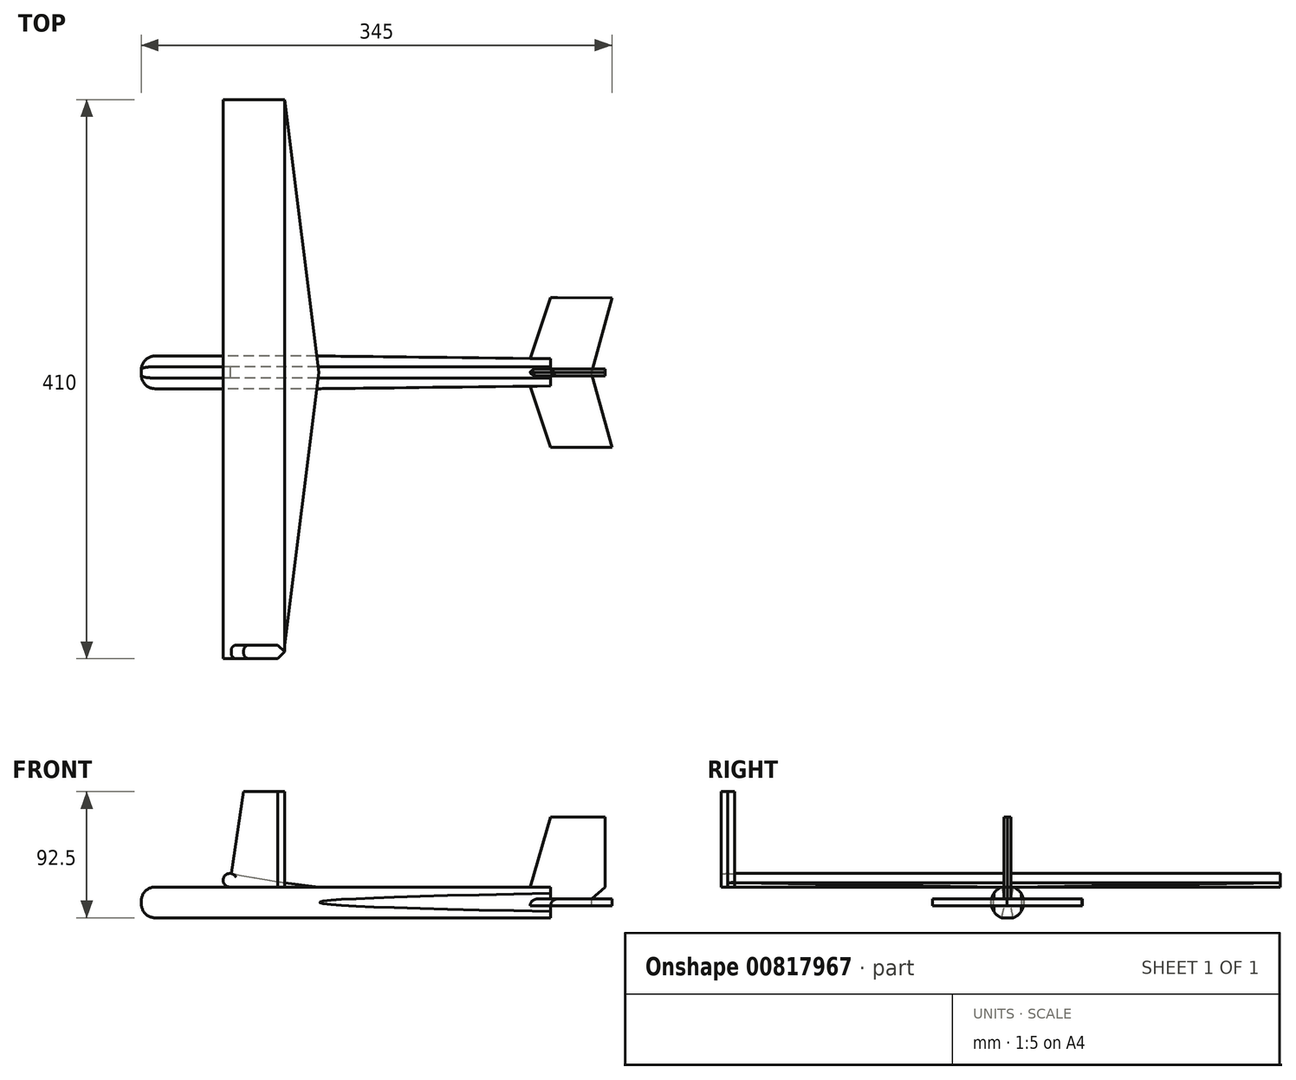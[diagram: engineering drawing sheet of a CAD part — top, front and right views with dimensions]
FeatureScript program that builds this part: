
annotation { "Feature Type Name" : "Feature", "Feature Type Description" : "" }
export const myFeature = defineFeature(function(context is Context, id is Id, definition is map)
    precondition{}
    {
        {
            var Q0;
            Q0=qCreatedBy(makeId("Top.planeOp"),FACE);
            var sketch = newSketch(context, id + "F0", { "sketchPlane" : qUnion([Q0])});
            skLineSegment(sketch, "E0", {"start": v(0, 0) * mm, "end": v(0, 200) * mm});
            skLineSegment(sketch, "E1", {"start": v(0, 0) * mm, "end": v(0, -200) * mm});
            skLineSegment(sketch, "E2", {"start": v(0, -200) * mm, "end": v(45, -200) * mm});
            skLineSegment(sketch, "E3", {"start": v(0, 200) * mm, "end": v(45, 200) * mm});
            skLineSegment(sketch, "E4", {"start": v(0, 0) * mm, "end": v(70, 0) * mm, "construction": true});
            skLineSegment(sketch, "E5", {"start": v(45, 200) * mm, "end": v(70, 0) * mm});
            skLineSegment(sketch, "E6", {"start": v(45, -200) * mm, "end": v(70, 0) * mm});
            skSolve(sketch);
        }
        {
            var Q0;
            Q0=makeQuery(id+"F0.imprint","IMPRINT",FACE,{"disambiguationData":[TD([[makeQuery(id+"F0.imprint","IMPRINT",EDGE,{"derivedFrom":sQuery(id+"F0.wireOp",EDGE,"E0")}),-1.0]])]});
            extrude(context, id + "F1", {"entities" : qUnion([Q0]), "depth" : 10 * mm, "offsetDistance" : 25 * mm});
        }
        {
            var Q0;
            Q0=makeQuery(id+"F1.opExtrude","SWEPT_FACE",FACE,{"disambiguationData":[OSD([sQuery(id+"F0.wireOp",EDGE,"E2")])]});
            var sketch = newSketch(context, id + "F2", { "sketchPlane" : qUnion([Q0])});
            skLineSegment(sketch, "E7.0.0", {"start": v(0, 0) * mm, "end": v(45, 0) * mm});
            skLineSegment(sketch, "E7.0.1", {"start": v(45, 0) * mm, "end": v(45, 10) * mm});
            skLineSegment(sketch, "E7.0.2", {"start": v(45, 10) * mm, "end": v(0, 10) * mm});
            skLineSegment(sketch, "E7.0.3", {"start": v(0, 10) * mm, "end": v(0, 5) * mm});
            skLineSegment(sketch, "E8.0.0", {"start": v(45, 0) * mm, "end": v(70, 0) * mm});
            skLineSegment(sketch, "E8.0.1", {"start": v(70, 0) * mm, "end": v(70, 10) * mm});
            skLineSegment(sketch, "E8.0.2", {"start": v(70, 10) * mm, "end": v(45, 10) * mm});
            skLineSegment(sketch, "E8.0.3", {"start": v(45, 10) * mm, "end": v(45, 0) * mm});
            skArc(sketch, "E9", {"start": v(5.87, 9.92) * mm, "mid": v(0.02, 5.44) * mm, "end": v(5, 0) * mm});
            skPoint(sketch, "E9.centerSnap0", {"position": v(0, 5) * mm});
            skLineSegment(sketch, "E10", {"start": v(5.87, 9.92) * mm, "end": v(45, 3) * mm});
            skLineSegment(sketch, "E11", {"start": v(45, 3) * mm, "end": v(70, 0) * mm});
            skSolve(sketch);
        }
        {
            var Q0;
            {var subQ5=sQuery(id+"F2.wireOp",EDGE,"E10");Q0=makeQuery(id+"F2.imprint","IMPRINT",FACE,{"disambiguationData":[TD([[makeQuery(id+"F2.imprint","IMPRINT",EDGE,{"derivedFrom":subQ5}),1.0]])]});}
            var Q1;
            Q1=makeQuery(id+"F2.imprint","IMPRINT",FACE,{"disambiguationData":[TD([[makeQuery(id+"F2.imprint","IMPRINT",EDGE,{"derivedFrom":sQuery(id+"F2.wireOp",EDGE,"E8.0.1")}),1.0]])]});
            var Q2;
            {var subQ0=sQuery(id+"F2.wireOp",EDGE,"E7.0.3");Q2=makeQuery(id+"F2.imprint","IMPRINT",FACE,{"disambiguationData":[TD([[makeQuery(id+"F2.imprint","IMPRINT",EDGE,{"derivedFrom":subQ0}),1.0]])]});}
            var Q3;
            {var subQ0=sQuery(id+"F2.wireOp",EDGE,"E7.0.0");var subQ3=sQuery(id+"F2.wireOp",EDGE,"E9");var subQ4=makeQuery(id+"F2.imprint","INTERSECT",VERTEX,{"derivedFrom":[subQ0,subQ3]});Q3=makeQuery(id+"F2.imprint","IMPRINT",FACE,{"disambiguationData":[TD([[makeQuery(id+"F2.imprint","IMPRINT",EDGE,{"disambiguationData":[TD([[subQ4,1.0]])],"derivedFrom":subQ0}),1.0]])]});}
            extrude(context, id + "F3", {"entities" : qUnion([Q0, Q1, Q2, Q3]), "operationType" : NewBodyOperationType.REMOVE, "oppositeDirection" : true, "depth" : 400 * mm, "offsetDistance" : 25 * mm});
        }
        {
            var Q0;
            Q0=qCreatedBy(makeId("Top.planeOp"),FACE);
            var sketch = newSketch(context, id + "F4", { "sketchPlane" : qUnion([Q0])});
            skLineSegment(sketch, "E12", {"start": v(0, 12) * mm, "end": v(0, -12) * mm});
            skLineSegment(sketch, "E13", {"start": v(0, -12) * mm, "end": v(-60, -12) * mm});
            skLineSegment(sketch, "E14", {"start": v(-60, -12) * mm, "end": v(-60, 12) * mm});
            skLineSegment(sketch, "E15", {"start": v(-60, 12) * mm, "end": v(0, 12) * mm});
            skLineSegment(sketch, "E16", {"start": v(0, -12) * mm, "end": v(70, -12) * mm});
            skLineSegment(sketch, "E17", {"start": v(70, -12) * mm, "end": v(70, 12) * mm});
            skLineSegment(sketch, "E18", {"start": v(70, 12) * mm, "end": v(0, 12) * mm});
            skLineSegment(sketch, "E19", {"start": v(0, 0) * mm, "end": v(240, 0) * mm, "construction": true});
            skPoint(sketch, "E19.endSnap0", {"position": v(70, 0) * mm});
            skLineSegment(sketch, "E20", {"start": v(240, -10) * mm, "end": v(240, 10) * mm});
            skLineSegment(sketch, "E21", {"start": v(240, -10) * mm, "end": v(70, -12) * mm});
            skLineSegment(sketch, "E22", {"start": v(70, 12) * mm, "end": v(240, 10) * mm});
            skSolve(sketch);
        }
        {
            var Q0;
            Q0=makeQuery(id+"F4.imprint","IMPRINT",FACE,{"disambiguationData":[TD([[makeQuery(id+"F4.imprint","IMPRINT",EDGE,{"derivedFrom":sQuery(id+"F4.wireOp",EDGE,"E12")}),1.0]])]});
            var Q1;
            Q1=makeQuery(id+"F4.imprint","IMPRINT",FACE,{"disambiguationData":[TD([[makeQuery(id+"F4.imprint","IMPRINT",EDGE,{"derivedFrom":sQuery(id+"F4.wireOp",EDGE,"E12")}),-1.0]])]});
            var Q2;
            Q2=makeQuery(id+"F4.imprint","IMPRINT",FACE,{"disambiguationData":[TD([[makeQuery(id+"F4.imprint","IMPRINT",EDGE,{"derivedFrom":sQuery(id+"F4.wireOp",EDGE,"E17")}),-1.0]])]});
            extrude(context, id + "F5", {"entities" : qUnion([Q0, Q1, Q2]), "operationType" : NewBodyOperationType.ADD, "oppositeDirection" : true, "depth" : 22.5 * mm, "offsetDistance" : 25 * mm});
        }
        {
            var Q0;
            Q0=makeQuery(id+"F5.opExtrude","SWEPT_FACE",FACE,{"disambiguationData":[OSD([sQuery(id+"F4.wireOp",EDGE,"E14")])]});
            var sketch = newSketch(context, id + "F6", { "sketchPlane" : qUnion([Q0])});
            skLineSegment(sketch, "E23.0.0", {"start": v(12, 0) * mm, "end": v(-12, 0) * mm});
            skLineSegment(sketch, "E23.0.1", {"start": v(-12, 0) * mm, "end": v(-12, -22.5) * mm});
            skLineSegment(sketch, "E23.0.2", {"start": v(-12, -22.5) * mm, "end": v(12, -22.5) * mm});
            skLineSegment(sketch, "E23.0.3", {"start": v(12, -22.5) * mm, "end": v(12, 0) * mm});
            skCircle(sketch, "E24", {"center": v(0, -11.25) * mm, "radius": 12 * mm});
            skPoint(sketch, "E24.centerSnap0", {"position": v(-12, -11.25) * mm});
            skSolve(sketch);
        }
        {
            var Q0;
            {var subQ0=sQuery(id+"F6.wireOp",EDGE,"E23.0.1");var subQ1=sQuery(id+"F6.wireOp",EDGE,"E23.0.0");var subQ2=makeQuery(id+"F6.imprint","INTERSECT",VERTEX,{"derivedFrom":[subQ1,subQ0]});Q0=makeQuery(id+"F6.imprint","IMPRINT",FACE,{"disambiguationData":[TD([[makeQuery(id+"F6.imprint","IMPRINT",EDGE,{"disambiguationData":[TD([[subQ2,1.0]])],"derivedFrom":subQ1}),1.0]])]});}
            var Q1;
            {var subQ0=sQuery(id+"F6.wireOp",EDGE,"E23.0.3");var subQ1=sQuery(id+"F6.wireOp",EDGE,"E23.0.0");var subQ2=makeQuery(id+"F6.imprint","INTERSECT",VERTEX,{"derivedFrom":[subQ1,subQ0]});Q1=makeQuery(id+"F6.imprint","IMPRINT",FACE,{"disambiguationData":[TD([[makeQuery(id+"F6.imprint","IMPRINT",EDGE,{"disambiguationData":[TD([[subQ2,-1.0]])],"derivedFrom":subQ1}),1.0]])]});}
            var Q2;
            {var subQ0=sQuery(id+"F6.wireOp",EDGE,"E23.0.3");var subQ1=sQuery(id+"F6.wireOp",EDGE,"E23.0.2");var subQ2=makeQuery(id+"F6.imprint","INTERSECT",VERTEX,{"derivedFrom":[subQ1,subQ0]});Q2=makeQuery(id+"F6.imprint","IMPRINT",FACE,{"disambiguationData":[TD([[makeQuery(id+"F6.imprint","IMPRINT",EDGE,{"disambiguationData":[TD([[subQ2,-1.0]])],"derivedFrom":subQ1}),-1.0]])]});}
            var Q3;
            {var subQ0=sQuery(id+"F6.wireOp",EDGE,"E23.0.2");var subQ1=sQuery(id+"F6.wireOp",EDGE,"E23.0.1");var subQ2=makeQuery(id+"F6.imprint","INTERSECT",VERTEX,{"derivedFrom":[subQ1,subQ0]});Q3=makeQuery(id+"F6.imprint","IMPRINT",FACE,{"disambiguationData":[TD([[makeQuery(id+"F6.imprint","IMPRINT",EDGE,{"disambiguationData":[TD([[subQ2,-1.0]])],"derivedFrom":subQ1}),-1.0]])]});}
            extrude(context, id + "F7", {"entities" : qUnion([Q0, Q1, Q2, Q3]), "operationType" : NewBodyOperationType.REMOVE, "oppositeDirection" : true, "depth" : 300 * mm, "offsetDistance" : 25 * mm});
        }
        {
            var Q0;
            Q0=makeQuery(id+"F5.opExtrude","SWEPT_FACE",FACE,{"disambiguationData":[OSD([sQuery(id+"F4.wireOp",EDGE,"E14")])]});
            fillet(context, id + "F8", {"entities" : qUnion([Q0]), "radius" : 10 * mm, "tangentPropagation" : true, "allowEdgeOverflow" : false});
        }
        {
            var Q0;
            {var subQ0=sQuery(id+"F0.wireOp",EDGE,"E5");var subQ2=sQuery(id+"F4.wireOp",EDGE,"E21");var subQ3=sQuery(id+"F4.wireOp",EDGE,"E16");var subQ4=sQuery(id+"F4.wireOp",EDGE,"E13");var subQ5=sQuery(id+"F4.wireOp",EDGE,"E18");var subQ6=sQuery(id+"F4.wireOp",EDGE,"E15");var subQ7=sQuery(id+"F4.wireOp",EDGE,"E20");var subQ8=sQuery(id+"F4.wireOp",EDGE,"E22");Q0=makeQuery(id+"F5.boolean.opBoolean","SPLIT",FACE,{"disambiguationData":[TD([makeQuery(id+"F1.opExtrude","SWEPT_FACE",FACE,{"disambiguationData":[OSD([subQ0])]})])],"derivedFrom":makeQuery(id+"F5.opExtrude","CAP_FACE",FACE,{"disambiguationData":[OSD([subQ4,sQuery(id+"F4.wireOp",EDGE,"E14"),subQ6,subQ3,subQ5,subQ7,subQ2,subQ8])],"isStart":true})});}
            cPlane(context, id + "F9", {"entities" : qUnion([Q0]), "cplaneType" : CPlaneType.OFFSET, "offset" : 11.25 * mm, "oppositeDirection" : true, "width" : 150 * mm, "height" : 150 * mm});
        }
        {
            var Q0;
            Q0=qCreatedBy(id+"F9.planeOp",FACE);
            var sketch = newSketch(context, id + "F10", { "sketchPlane" : qUnion([Q0])});
            skLineSegment(sketch, "E25.0", {"start": v(240, 10) * mm, "end": v(70, 12) * mm});
            skLineSegment(sketch, "E26.0", {"start": v(240, -4.18) * mm, "end": v(240, 4.18) * mm});
            skLineSegment(sketch, "E27.0", {"start": v(240, 4.18) * mm, "end": v(240, 10) * mm});
            skLineSegment(sketch, "E28.0", {"start": v(240, -10) * mm, "end": v(240, -4.18) * mm});
            skLineSegment(sketch, "E29.0", {"start": v(240, -10) * mm, "end": v(70, -12) * mm});
            skLineSegment(sketch, "E30", {"start": v(240, 0) * mm, "end": v(225, 0.18) * mm, "construction": true});
            skLineSegment(sketch, "E31", {"start": v(240, 0) * mm, "end": v(270, -0.35) * mm, "construction": true});
            skPoint(sketch, "E32", {"position": v(230, 0.12) * mm});
            skLineSegment(sketch, "E33", {"start": v(230, 0.12) * mm, "end": v(230, 10.12) * mm, "construction": true});
            skLineSegment(sketch, "E34", {"start": v(230, 0.12) * mm, "end": v(230, -10.12) * mm, "construction": true});
            skLineSegment(sketch, "E35", {"start": v(225, -10.18) * mm, "end": v(225, 10.18) * mm, "construction": true});
            skLineSegment(sketch, "E36", {"start": v(240, 0) * mm, "end": v(240, 55) * mm, "construction": true});
            skLineSegment(sketch, "E37", {"start": v(240, 0) * mm, "end": v(240, -55) * mm, "construction": true});
            skLineSegment(sketch, "E38", {"start": v(240, -55) * mm, "end": v(285, -55) * mm});
            skLineSegment(sketch, "E39", {"start": v(285, -55) * mm, "end": v(270, -0.35) * mm});
            skLineSegment(sketch, "E40", {"start": v(240, 55) * mm, "end": v(285, 54.47) * mm});
            skLineSegment(sketch, "E41", {"start": v(285, 54.47) * mm, "end": v(270, -0.35) * mm});
            skLineSegment(sketch, "E42", {"start": v(240, 55) * mm, "end": v(225, 10.18) * mm});
            skLineSegment(sketch, "E43", {"start": v(240, -55) * mm, "end": v(225, -10.18) * mm});
            skSolve(sketch);
        }
        {
            var Q0;
            Q0=makeQuery(id+"F10.imprint","IMPRINT",FACE,{"disambiguationData":[TD([[makeQuery(id+"F10.imprint","IMPRINT",EDGE,{"derivedFrom":sQuery(id+"F10.wireOp",EDGE,"E26.0")}),-1.0]])]});
            extrude(context, id + "F11", {"entities" : qUnion([Q0]), "operationType" : NewBodyOperationType.ADD, "endBound" : BoundingType.SYMMETRIC, "depth" : 5 * mm, "offsetDistance" : 25 * mm});
        }
        {
            var Q0;
            Q0=qCreatedBy(makeId("Front.planeOp"),FACE);
            var sketch = newSketch(context, id + "F12", { "sketchPlane" : qUnion([Q0])});
            skLineSegment(sketch, "E44.0", {"start": v(240, -8.75) * mm, "end": v(285, -8.75) * mm});
            skLineSegment(sketch, "E45.0", {"start": v(240, -8.75) * mm, "end": v(240, -4.62) * mm});
            skLineSegment(sketch, "E46.0", {"start": v(240, -4.62) * mm, "end": v(240, 0) * mm});
            skLineSegment(sketch, "E47.0", {"start": v(240, 0) * mm, "end": v(69.48, 0) * mm});
            skLineSegment(sketch, "E48.0", {"start": v(240, -8.75) * mm, "end": v(225, -8.75) * mm});
            skLineSegment(sketch, "E49", {"start": v(225, -8.75) * mm, "end": v(225, 0) * mm, "construction": true});
            skLineSegment(sketch, "E50", {"start": v(240, -8.75) * mm, "end": v(240, 51.25) * mm, "construction": true});
            skPoint(sketch, "E51", {"position": v(270, -8.75) * mm});
            skLineSegment(sketch, "E52", {"start": v(225, 0) * mm, "end": v(240, 51.25) * mm});
            skLineSegment(sketch, "E53", {"start": v(280, 51.25) * mm, "end": v(240, 51.25) * mm});
            skLineSegment(sketch, "E54", {"start": v(280, 0) * mm, "end": v(270, -8.75) * mm});
            skLineSegment(sketch, "E55", {"start": v(280, 51.25) * mm, "end": v(280, 0) * mm});
            skSolve(sketch);
        }
        {
            var Q0;
            {var subQ3=sQuery(id+"F12.wireOp",EDGE,"E45.0");Q0=makeQuery(id+"F12.imprint","IMPRINT",FACE,{"disambiguationData":[TD([[makeQuery(id+"F12.imprint","IMPRINT",EDGE,{"derivedFrom":subQ3}),-1.0]])]});}
            extrude(context, id + "F13", {"entities" : qUnion([Q0]), "operationType" : NewBodyOperationType.ADD, "endBound" : BoundingType.SYMMETRIC, "depth" : 5 * mm, "offsetDistance" : 25 * mm, "hasDraft" : true, "draftAngle" : 3 * degree});
        }
        {
            var Q0;
            Q0=makeQuery(id+"F11.opExtrude","CAP_EDGE",EDGE,{"disambiguationData":[OSD([sQuery(id+"F10.wireOp",EDGE,"E42")])],"isStart":false});
            var Q1;
            Q1=makeQuery(id+"F11.opExtrude","CAP_EDGE",EDGE,{"disambiguationData":[OSD([sQuery(id+"F10.wireOp",EDGE,"E43")])],"isStart":false});
            fillet(context, id + "F14", {"entities" : qUnion([Q0, Q1]), "radius" : 5 * mm, "tangentPropagation" : true, "allowEdgeOverflow" : false});
        }
        {
            var Q0;
            Q0=makeQuery(id+"F13.opExtrude","CAP_EDGE",EDGE,{"disambiguationData":[OSD([sQuery(id+"F12.wireOp",EDGE,"E52")])],"isStart":true});
            var Q1;
            Q1=makeQuery(id+"F13.opExtrude","CAP_EDGE",EDGE,{"disambiguationData":[OSD([sQuery(id+"F12.wireOp",EDGE,"E52")])],"isStart":false});
            fillet(context, id + "F15", {"entities" : qUnion([Q0, Q1]), "radius" : 5 * mm, "tangentPropagation" : true, "allowEdgeOverflow" : false});
        }
        {
            var Q0;
            Q0=makeQuery(id+"F1.opExtrude","SWEPT_FACE",FACE,{"disambiguationData":[OSD([sQuery(id+"F0.wireOp",EDGE,"E2")])]});
            var sketch = newSketch(context, id + "F16", { "sketchPlane" : qUnion([Q0])});
            skArc(sketch, "E56", {"start": v(5.87, 9.92) * mm, "mid": v(0.02, 5.44) * mm, "end": v(5, 0) * mm});
            skLineSegment(sketch, "E57", {"start": v(5, 0) * mm, "end": v(5.87, 9.92) * mm});
            skSolve(sketch);
        }
        {
            var Q0;
            Q0=qSketchRegion(id+"F16",true);
            extrude(context, id + "F17", {"entities" : qUnion([Q0]), "operationType" : NewBodyOperationType.ADD, "depth" : 10 * mm, "offsetDistance" : 25 * mm});
        }
        {
            var Q0;
            Q0=makeQuery(id+"F1.opExtrude","SWEPT_FACE",FACE,{"disambiguationData":[OSD([sQuery(id+"F0.wireOp",EDGE,"E2")])]});
            var sketch = newSketch(context, id + "F18", { "sketchPlane" : qUnion([Q0])});
            skLineSegment(sketch, "E58", {"start": v(45, 0) * mm, "end": v(45, 70) * mm});
            skLineSegment(sketch, "E59", {"start": v(45, 70) * mm, "end": v(15, 70) * mm});
            skLineSegment(sketch, "E60", {"start": v(15, 70) * mm, "end": v(5.87, 9.92) * mm});
            skLineSegment(sketch, "E61", {"start": v(5.87, 9.92) * mm, "end": v(5, 0) * mm});
            skLineSegment(sketch, "E62", {"start": v(5, 0) * mm, "end": v(45, 0) * mm});
            skSolve(sketch);
        }
        {
            var Q0;
            Q0=qSketchRegion(id+"F18",true);
            extrude(context, id + "F19", {"entities" : qUnion([Q0]), "operationType" : NewBodyOperationType.ADD, "depth" : 10 * mm, "offsetDistance" : 25 * mm});
        }
        {
            var Q0;
            Q0=makeQuery(id+"F19.opExtrude","CAP_EDGE",EDGE,{"disambiguationData":[OSD([sQuery(id+"F18.wireOp",EDGE,"E60")])],"isStart":true});
            var Q1;
            Q1=makeQuery(id+"F19.opExtrude","CAP_EDGE",EDGE,{"disambiguationData":[OSD([sQuery(id+"F18.wireOp",EDGE,"E60")])],"isStart":false});
            fillet(context, id + "F20", {"entities" : qUnion([Q0, Q1]), "radius" : 4 * mm, "tangentPropagation" : true, "allowEdgeOverflow" : false});
        }
        {
            var Q0;
            Q0=makeQuery(id+"F19.opExtrude","CAP_EDGE",EDGE,{"disambiguationData":[OSD([sQuery(id+"F18.wireOp",EDGE,"E58")])],"isStart":false});
            var Q1;
            Q1=makeQuery(id+"F19.boolean.opBoolean","SPLIT",EDGE,{"derivedFrom":makeQuery(id+"F19.opExtrude","CAP_EDGE",EDGE,{"disambiguationData":[OSD([sQuery(id+"F18.wireOp",EDGE,"E58")])],"isStart":true})});
            chamfer(context, id + "F21", {"entities" : qUnion([Q0, Q1]), "width" : 5 * mm, "tangentPropagation" : true});
        }
    });
